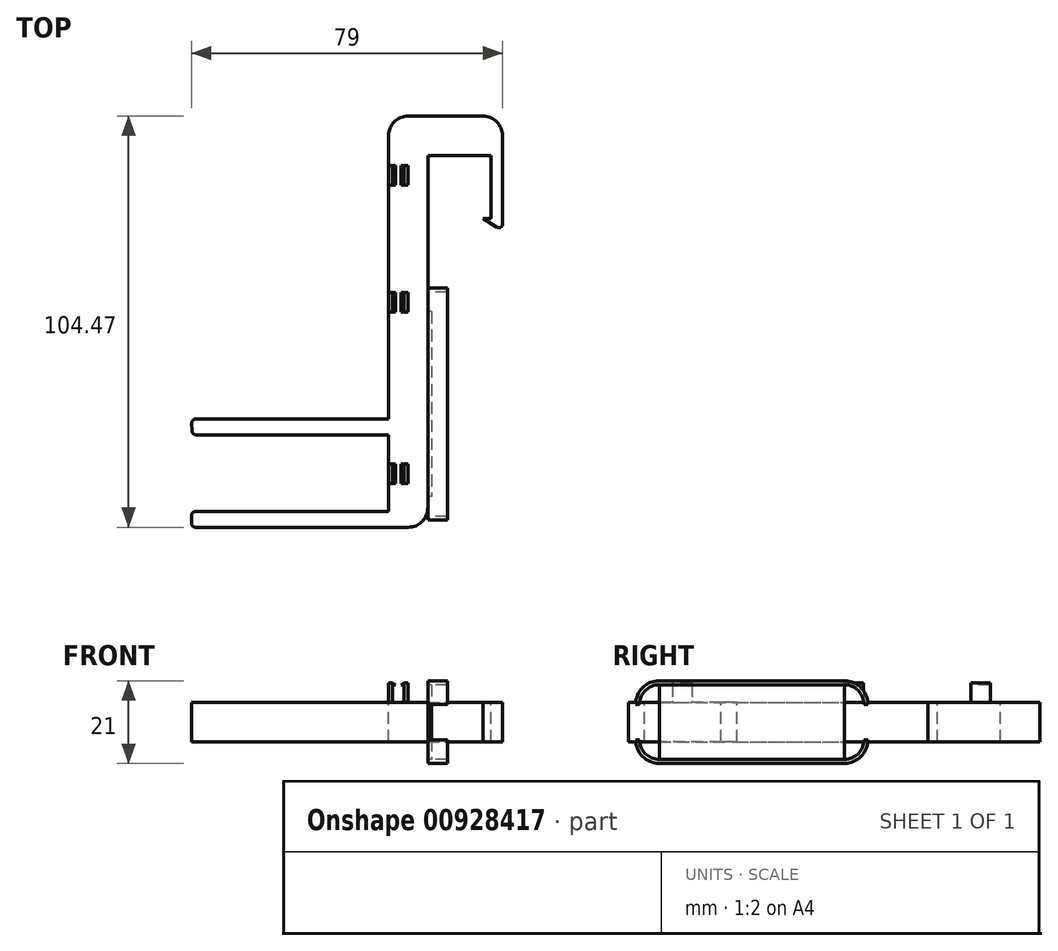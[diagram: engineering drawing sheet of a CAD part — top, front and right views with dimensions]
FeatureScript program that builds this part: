
annotation { "Feature Type Name" : "Feature", "Feature Type Description" : "" }
export const myFeature = defineFeature(function(context is Context, id is Id, definition is map)
    precondition{}
    {
        {
            var Q0;
            Q0=qCreatedBy(makeId("Top.planeOp"),FACE);
            var sketch = newSketch(context, id + "F0", { "sketchPlane" : qUnion([Q0])});
            skLineSegment(sketch, "E0.left", {"start": v(0, 0) * mm, "end": v(0, 75.97) * mm});
            skLineSegment(sketch, "E0.right", {"start": v(10, -18.5) * mm, "end": v(10, 71) * mm});
            skLineSegment(sketch, "E1.bottom", {"start": v(10, 71) * mm, "end": v(26, 71) * mm});
            skLineSegment(sketch, "E1.top", {"start": v(5, 80.97) * mm, "end": v(24, 80.97) * mm});
            skLineSegment(sketch, "E2.bottom", {"start": v(26, 71) * mm, "end": v(29, 71) * mm});
            skLineSegment(sketch, "E2.top", {"start": v(26, 55) * mm, "end": v(29, 55) * mm});
            skLineSegment(sketch, "E2.left", {"start": v(26, 71) * mm, "end": v(26, 55) * mm});
            skLineSegment(sketch, "E2.right", {"start": v(29, 71) * mm, "end": v(29, 55) * mm});
            skLineSegment(sketch, "E3", {"start": v(26, 55) * mm, "end": v(24.07, 55) * mm});
            skLineSegment(sketch, "E4", {"start": v(24.07, 55) * mm, "end": v(27.45, 52.77) * mm});
            skLineSegment(sketch, "E5", {"start": v(29, 53.6) * mm, "end": v(29, 55) * mm});
            skLineSegment(sketch, "E6", {"start": v(29, 75.97) * mm, "end": v(29, 71) * mm});
            skPoint(sketch, "E7.visualSharp", {"position": v(0, 80.97) * mm});
            skArc(sketch, "E7.filletArc", {"start": v(5, 80.97) * mm, "mid": v(1.46, 79.5) * mm, "end": v(0, 75.97) * mm});
            skPoint(sketch, "E8.visualSharp", {"position": v(29, 80.97) * mm});
            skArc(sketch, "E8.filletArc", {"start": v(29, 75.97) * mm, "mid": v(27.54, 79.5) * mm, "end": v(24, 80.97) * mm});
            skLineSegment(sketch, "E9.bottom", {"start": v(0, 0) * mm, "end": v(-48.89, 0) * mm});
            skLineSegment(sketch, "E9.top", {"start": v(0, 4) * mm, "end": v(-48.96, 4) * mm});
            skLineSegment(sketch, "E9.left", {"start": v(0, 0) * mm, "end": v(0, 4) * mm});
            skLineSegment(sketch, "E10.right", {"start": v(0, 0) * mm, "end": v(0, -19.5) * mm});
            skLineSegment(sketch, "E11.bottom", {"start": v(-49, -19.5) * mm, "end": v(0, -19.5) * mm});
            skLineSegment(sketch, "E11.top", {"start": v(-49, -23.5) * mm, "end": v(0, -23.5) * mm});
            skLineSegment(sketch, "E11.left", {"start": v(-50, -20.5) * mm, "end": v(-50, -22.5) * mm});
            skLineSegment(sketch, "E11.right", {"start": v(0, -19.5) * mm, "end": v(0, -23.5) * mm});
            skLineSegment(sketch, "E12", {"start": v(0, -23.5) * mm, "end": v(5, -23.5) * mm});
            skPoint(sketch, "E13.visualSharp", {"position": v(10, -23.5) * mm});
            skArc(sketch, "E13.filletArc", {"start": v(5, -23.5) * mm, "mid": v(8.54, -22.04) * mm, "end": v(10, -18.5) * mm});
            skPoint(sketch, "E14.visualSharp", {"position": v(-50, -23.5) * mm});
            skPoint(sketch, "E15.visualSharp", {"position": v(-50, -19.5) * mm});
            skArc(sketch, "E15.filletArc", {"start": v(-49, -19.5) * mm, "mid": v(-49.7, -19.8) * mm, "end": v(-50, -20.5) * mm});
            skArc(sketch, "E16.filletArc", {"start": v(-50, -22.5) * mm, "mid": v(-49.7, -23.2) * mm, "end": v(-49, -23.5) * mm});
            skPoint(sketch, "E17.visualSharp", {"position": v(29, 51.74) * mm});
            skArc(sketch, "E17.filletArc", {"start": v(27.45, 52.77) * mm, "mid": v(28.47, 52.72) * mm, "end": v(29, 53.6) * mm});
            skLineSegment(sketch, "E18", {"start": v(-49.96, 2.96) * mm, "end": v(-49.89, 0.96) * mm});
            skPoint(sketch, "E19.visualSharp", {"position": v(-50, 4) * mm});
            skArc(sketch, "E19.filletArc", {"start": v(-48.96, 4) * mm, "mid": v(-49.68, 3.7) * mm, "end": v(-49.96, 2.96) * mm});
            skPoint(sketch, "E20.visualSharp", {"position": v(-49.85, 0) * mm});
            skArc(sketch, "E20.filletArc", {"start": v(-49.89, 0.96) * mm, "mid": v(-49.58, 0.28) * mm, "end": v(-48.89, 0) * mm});
            skSolve(sketch);
        }
        {
            var Q0;
            Q0=makeQuery(id+"F0.imprint","IMPRINT",FACE,{"disambiguationData":[TD([[makeQuery(id+"F0.imprint","IMPRINT",EDGE,{"derivedFrom":sQuery(id+"F0.wireOp",EDGE,"E11.bottom")}),-1.0]])]});
            var Q1;
            Q1=makeQuery(id+"F0.imprint","IMPRINT",FACE,{"disambiguationData":[TD([[makeQuery(id+"F0.imprint","IMPRINT",EDGE,{"derivedFrom":sQuery(id+"F0.wireOp",EDGE,"E0.left")}),-1.0]])]});
            var Q2;
            Q2=makeQuery(id+"F0.imprint","IMPRINT",FACE,{"disambiguationData":[TD([[makeQuery(id+"F0.imprint","IMPRINT",EDGE,{"derivedFrom":sQuery(id+"F0.wireOp",EDGE,"E2.bottom")}),-1.0]])]});
            var Q3;
            Q3=makeQuery(id+"F0.imprint","IMPRINT",FACE,{"disambiguationData":[TD([[makeQuery(id+"F0.imprint","IMPRINT",EDGE,{"derivedFrom":sQuery(id+"F0.wireOp",EDGE,"E9.bottom")}),-1.0]])]});
            var Q4;
            Q4=makeQuery(id+"F0.imprint","IMPRINT",FACE,{"disambiguationData":[TD([[makeQuery(id+"F0.imprint","IMPRINT",EDGE,{"derivedFrom":sQuery(id+"F0.wireOp",EDGE,"E2.top")}),-1.0]])]});
            extrude(context, id + "F1", {"entities" : qUnion([Q0, Q1, Q2, Q3, Q4]), "oppositeDirection" : true, "depth" : 10 * mm, "offsetDistance" : 25 * mm});
        }
        {
            var Q0;
            Q0=makeQuery(id+"F0.imprint","IMPRINT",FACE,{"disambiguationData":[TD([[makeQuery(id+"F0.imprint","IMPRINT",EDGE,{"derivedFrom":sQuery(id+"F0.wireOp",EDGE,"E0.left")}),-1.0]])]});
            var sketch = newSketch(context, id + "F2", { "sketchPlane" : qUnion([Q0])});
            skLineSegment(sketch, "E21.bottom", {"start": v(0, -12.36) * mm, "end": v(1, -12.36) * mm});
            skLineSegment(sketch, "E21.top", {"start": v(0, -7.36) * mm, "end": v(1, -7.36) * mm});
            skLineSegment(sketch, "E21.left", {"start": v(0, -12.36) * mm, "end": v(0, -7.36) * mm});
            skLineSegment(sketch, "E21.right", {"start": v(1, -12.36) * mm, "end": v(1, -7.36) * mm});
            skSolve(sketch);
        }
        {
            var Q0;
            Q0 = qSketchRegion(id + "F2", true);
            extrude(context, id + "F3", {"entities" : qUnion([Q0]), "depth" : 5 * mm, "offsetDistance" : 25 * mm});
        }
        {
            var Q0;
            Q0=makeQuery(id+"F3.opExtrude","SWEPT_FACE",FACE,{"disambiguationData":[OSD([sQuery(id+"F2.wireOp",EDGE,"E21.bottom")])]});
            var sketch = newSketch(context, id + "F4", { "sketchPlane" : qUnion([Q0])});
            skLineSegment(sketch, "E22", {"start": v(1, 5) * mm, "end": v(1.84, 4.4) * mm});
            skLineSegment(sketch, "E23", {"start": v(1.84, 4.4) * mm, "end": v(1, 4.4) * mm});
            skLineSegment(sketch, "E24", {"start": v(1, 4.4) * mm, "end": v(1, 5) * mm});
            skSolve(sketch);
        }
        {
            var Q0;
            Q0 = qSketchRegion(id + "F4", true);
            var Q1;
            Q1=makeQuery(id+"F3.opExtrude","SWEPT_FACE",FACE,{"disambiguationData":[OSD([sQuery(id+"F2.wireOp",EDGE,"E21.top")])]});
            extrude(context, id + "F5", {"entities" : qUnion([Q0]), "operationType" : NewBodyOperationType.ADD, "endBound" : BoundingType.UP_TO_SURFACE, "oppositeDirection" : true, "depth" : 25 * mm, "endBoundEntityFace" : qUnion([Q1]), "offsetDistance" : 25 * mm});
        }
        {
            var Q0;
            Q0=makeQuery(id+"F3.opExtrude","SWEPT_BODY",BODY,{"disambiguationData":[OSD([sQuery(id+"F2.wireOp",EDGE,"E21.bottom"),sQuery(id+"F2.wireOp",EDGE,"E21.top"),sQuery(id+"F2.wireOp",EDGE,"E21.left"),sQuery(id+"F2.wireOp",EDGE,"E21.right")])]});
            transform(context, id + "F6", {"entities" : qUnion([Q0]), "transformType" : TransformType.TRANSLATION_3D, "dx" : 0 * mm, "dy" : 43.5 * mm, "dz" : 0 * mm, "makeCopy" : true});
        }
        {
            var Q0;
            Q0=makeQuery(id+"F6.opPattern","COPY",BODY,{"derivedFrom":makeQuery(id+"F3.opExtrude","SWEPT_BODY",BODY,{"disambiguationData":[OSD([sQuery(id+"F2.wireOp",EDGE,"E21.bottom"),sQuery(id+"F2.wireOp",EDGE,"E21.top"),sQuery(id+"F2.wireOp",EDGE,"E21.left"),sQuery(id+"F2.wireOp",EDGE,"E21.right")])]}),"instanceName":"1"});
            transform(context, id + "F7", {"entities" : qUnion([Q0]), "transformType" : TransformType.TRANSLATION_3D, "dx" : 0 * mm, "dy" : 32.3 * mm, "dz" : 0 * mm, "makeCopy" : true});
        }
        {
            var Q0;
            Q0=makeQuery(id+"F1.opExtrude","SWEPT_FACE",FACE,{"disambiguationData":[OSD([sQuery(id+"F0.wireOp",EDGE,"E0.left")])]});
            cPlane(context, id + "F8", {"entities" : qUnion([Q0]), "cplaneType" : CPlaneType.OFFSET, "offset" : 2.5 * mm, "oppositeDirection" : true, "width" : 150 * mm, "height" : 150 * mm});
        }
        {
            var Q0;
            Q0=makeQuery(id+"F3.opExtrude","SWEPT_BODY",BODY,{"disambiguationData":[OSD([sQuery(id+"F2.wireOp",EDGE,"E21.bottom"),sQuery(id+"F2.wireOp",EDGE,"E21.top"),sQuery(id+"F2.wireOp",EDGE,"E21.left"),sQuery(id+"F2.wireOp",EDGE,"E21.right")])]});
            var Q1;
            Q1=makeQuery(id+"F6.opPattern","COPY",BODY,{"derivedFrom":makeQuery(id+"F3.opExtrude","SWEPT_BODY",BODY,{"disambiguationData":[OSD([sQuery(id+"F2.wireOp",EDGE,"E21.bottom"),sQuery(id+"F2.wireOp",EDGE,"E21.top"),sQuery(id+"F2.wireOp",EDGE,"E21.left"),sQuery(id+"F2.wireOp",EDGE,"E21.right")])]}),"instanceName":"1"});
            var Q2;
            Q2=makeQuery(id+"F7.opPattern","COPY",BODY,{"derivedFrom":makeQuery(id+"F6.opPattern","COPY",BODY,{"derivedFrom":makeQuery(id+"F3.opExtrude","SWEPT_BODY",BODY,{"disambiguationData":[OSD([sQuery(id+"F2.wireOp",EDGE,"E21.bottom"),sQuery(id+"F2.wireOp",EDGE,"E21.top"),sQuery(id+"F2.wireOp",EDGE,"E21.left"),sQuery(id+"F2.wireOp",EDGE,"E21.right")])]}),"instanceName":"1"}),"instanceName":"1"});
            var Q3;
            Q3=qCreatedBy(id+"F8.planeOp",FACE);
            mirror(context, id + "F9", {"operationType" : NewBodyOperationType.ADD, "entities" : qUnion([Q0, Q1, Q2]), "mirrorPlane" : qUnion([Q3])});
        }
        {
            var Q0;
            Q0=makeQuery(id+"F1.opExtrude","SWEPT_FACE",FACE,{"disambiguationData":[OSD([sQuery(id+"F0.wireOp",EDGE,"E0.right")])]});
            var sketch = newSketch(context, id + "F10", { "sketchPlane" : qUnion([Q0])});
            skLineSegment(sketch, "E25.bottom", {"start": v(31.3, -14.5) * mm, "end": v(-15.7, -14.5) * mm});
            skLineSegment(sketch, "E25.top", {"start": v(31.3, 4.5) * mm, "end": v(-15.7, 4.5) * mm});
            skPoint(sketch, "E25.middle", {"position": v(7.8, -5) * mm});
            skPoint(sketch, "E25.middle.positionSnap0", {"position": v(-18.5, -5) * mm});
            skPoint(sketch, "E25.centerSnap0", {"position": v(-18.5, -5) * mm});
            skPoint(sketch, "E26.visualSharp", {"position": v(38.3, -14.5) * mm});
            skArc(sketch, "E26.filletArc", {"start": v(31.3, -14.5) * mm, "mid": v(34.84, -13.04) * mm, "end": v(36.3, -9.5) * mm});
            skPoint(sketch, "E27.visualSharp", {"position": v(38.3, 4.5) * mm});
            skArc(sketch, "E27.filletArc", {"start": v(36.3, -0.5) * mm, "mid": v(34.84, 3.04) * mm, "end": v(31.3, 4.5) * mm});
            skPoint(sketch, "E28.visualSharp", {"position": v(-22.7, -14.5) * mm});
            skArc(sketch, "E28.filletArc", {"start": v(-20.7, -9.5) * mm, "mid": v(-19.23, -13.04) * mm, "end": v(-15.7, -14.5) * mm});
            skPoint(sketch, "E29.visualSharp", {"position": v(-22.7, 4.5) * mm});
            skArc(sketch, "E29.filletArc", {"start": v(-15.7, 4.5) * mm, "mid": v(-19.23, 3.04) * mm, "end": v(-20.7, -0.5) * mm});
            skArc(sketch, "E30.0", {"start": v(37.3, -0.5) * mm, "mid": v(35.55, 3.74) * mm, "end": v(31.3, 5.5) * mm});
            skLineSegment(sketch, "E30.2", {"start": v(31.3, 5.5) * mm, "end": v(-15.7, 5.5) * mm});
            skArc(sketch, "E30.3", {"start": v(31.3, -15.5) * mm, "mid": v(35.55, -13.74) * mm, "end": v(37.3, -9.5) * mm});
            skArc(sketch, "E30.4", {"start": v(-15.7, 5.5) * mm, "mid": v(-19.93, 3.74) * mm, "end": v(-21.7, -0.5) * mm});
            skArc(sketch, "E30.6", {"start": v(-21.7, -9.5) * mm, "mid": v(-19.93, -13.74) * mm, "end": v(-15.7, -15.5) * mm});
            skLineSegment(sketch, "E30.7", {"start": v(31.3, -15.5) * mm, "end": v(-15.7, -15.5) * mm});
            skLineSegment(sketch, "E31", {"start": v(37.3, -0.5) * mm, "end": v(36.3, -0.5) * mm});
            skLineSegment(sketch, "E32", {"start": v(37.3, -9.5) * mm, "end": v(36.3, -9.5) * mm});
            skLineSegment(sketch, "E33", {"start": v(-20.7, -0.5) * mm, "end": v(-21.7, -0.5) * mm});
            skLineSegment(sketch, "E34", {"start": v(-20.7, -9.5) * mm, "end": v(-21.7, -9.5) * mm});
            skLineSegment(sketch, "E35", {"start": v(-15.7, 4.5) * mm, "end": v(-15.7, -14.5) * mm});
            skLineSegment(sketch, "E36", {"start": v(31.3, 5.5) * mm, "end": v(31.3, -14.5) * mm});
            skSolve(sketch);
        }
        {
            var Q0;
            {var subQ5=sQuery(id+"F10.wireOp",EDGE,"E25.top");Q0=makeQuery(id+"F10.imprint","IMPRINT",FACE,{"disambiguationData":[TD([[makeQuery(id+"F10.imprint","IMPRINT",EDGE,{"derivedFrom":subQ5}),-1.0]])]});}
            var Q1;
            {var subQ0=sQuery(id+"F10.wireOp",EDGE,"E31");Q1=makeQuery(id+"F10.imprint","IMPRINT",FACE,{"disambiguationData":[TD([[makeQuery(id+"F10.imprint","IMPRINT",EDGE,{"derivedFrom":subQ0}),-1.0]])]});}
            var Q2;
            {var subQ0=sQuery(id+"F10.wireOp",EDGE,"E32");Q2=makeQuery(id+"F10.imprint","IMPRINT",FACE,{"disambiguationData":[TD([[makeQuery(id+"F10.imprint","IMPRINT",EDGE,{"derivedFrom":subQ0}),1.0]])]});}
            var Q3;
            {var subQ4=sQuery(id+"F10.wireOp",EDGE,"E25.bottom");Q3=makeQuery(id+"F10.imprint","IMPRINT",FACE,{"disambiguationData":[TD([[makeQuery(id+"F10.imprint","IMPRINT",EDGE,{"derivedFrom":subQ4}),1.0]])]});}
            var Q4;
            {var subQ3=makeQuery(id+"F1.opExtrude","CAP_EDGE",EDGE,{"disambiguationData":[OSD([sQuery(id+"F0.wireOp",EDGE,"E0.right")])],"isStart":true});var subQ5=sQuery(id+"F10.wireOp",EDGE,"E30.0");var subQ7=makeQuery(id+"F10.imprint","INTERSECT",VERTEX,{"derivedFrom":[subQ3,subQ5]});Q4=makeQuery(id+"F10.imprint","IMPRINT",FACE,{"disambiguationData":[TD([[makeQuery(id+"F10.imprint","IMPRINT",EDGE,{"disambiguationData":[TD([[subQ7,1.0]])],"derivedFrom":subQ3}),1.0]])]});}
            extrude(context, id + "F11", {"entities" : qUnion([Q0, Q1, Q2, Q3, Q4]), "operationType" : NewBodyOperationType.ADD, "depth" : 5 * mm, "offsetDistance" : 25 * mm});
        }
        {
            var Q0;
            {var subQ0=sQuery(id+"F10.wireOp",EDGE,"E25.top");Q0=makeQuery(id+"F10.imprint","IMPRINT",FACE,{"disambiguationData":[TD([[makeQuery(id+"F10.imprint","IMPRINT",EDGE,{"derivedFrom":subQ0}),1.0]])]});}
            var Q1;
            {var subQ0=sQuery(id+"F10.wireOp",EDGE,"E35");var subQ1=sQuery(id+"F0.wireOp",EDGE,"E0.right");var subQ2=makeQuery(id+"F1.opExtrude","CAP_EDGE",EDGE,{"disambiguationData":[OSD([subQ1])],"isStart":true});var subQ3=makeQuery(id+"F10.imprint","INTERSECT",VERTEX,{"derivedFrom":[subQ2,subQ0]});Q1=makeQuery(id+"F10.imprint","IMPRINT",FACE,{"disambiguationData":[TD([[makeQuery(id+"F10.imprint","IMPRINT",EDGE,{"disambiguationData":[TD([[subQ3,-1.0]])],"derivedFrom":subQ0}),1.0]])]});}
            var Q2;
            {var subQ0=sQuery(id+"F10.wireOp",EDGE,"E25.bottom");Q2=makeQuery(id+"F10.imprint","IMPRINT",FACE,{"disambiguationData":[TD([[makeQuery(id+"F10.imprint","IMPRINT",EDGE,{"derivedFrom":subQ0}),-1.0]])]});}
            extrude(context, id + "F12", {"entities" : qUnion([Q0, Q1, Q2]), "depth" : 1 * mm, "offsetDistance" : 25 * mm});
        }
    });
